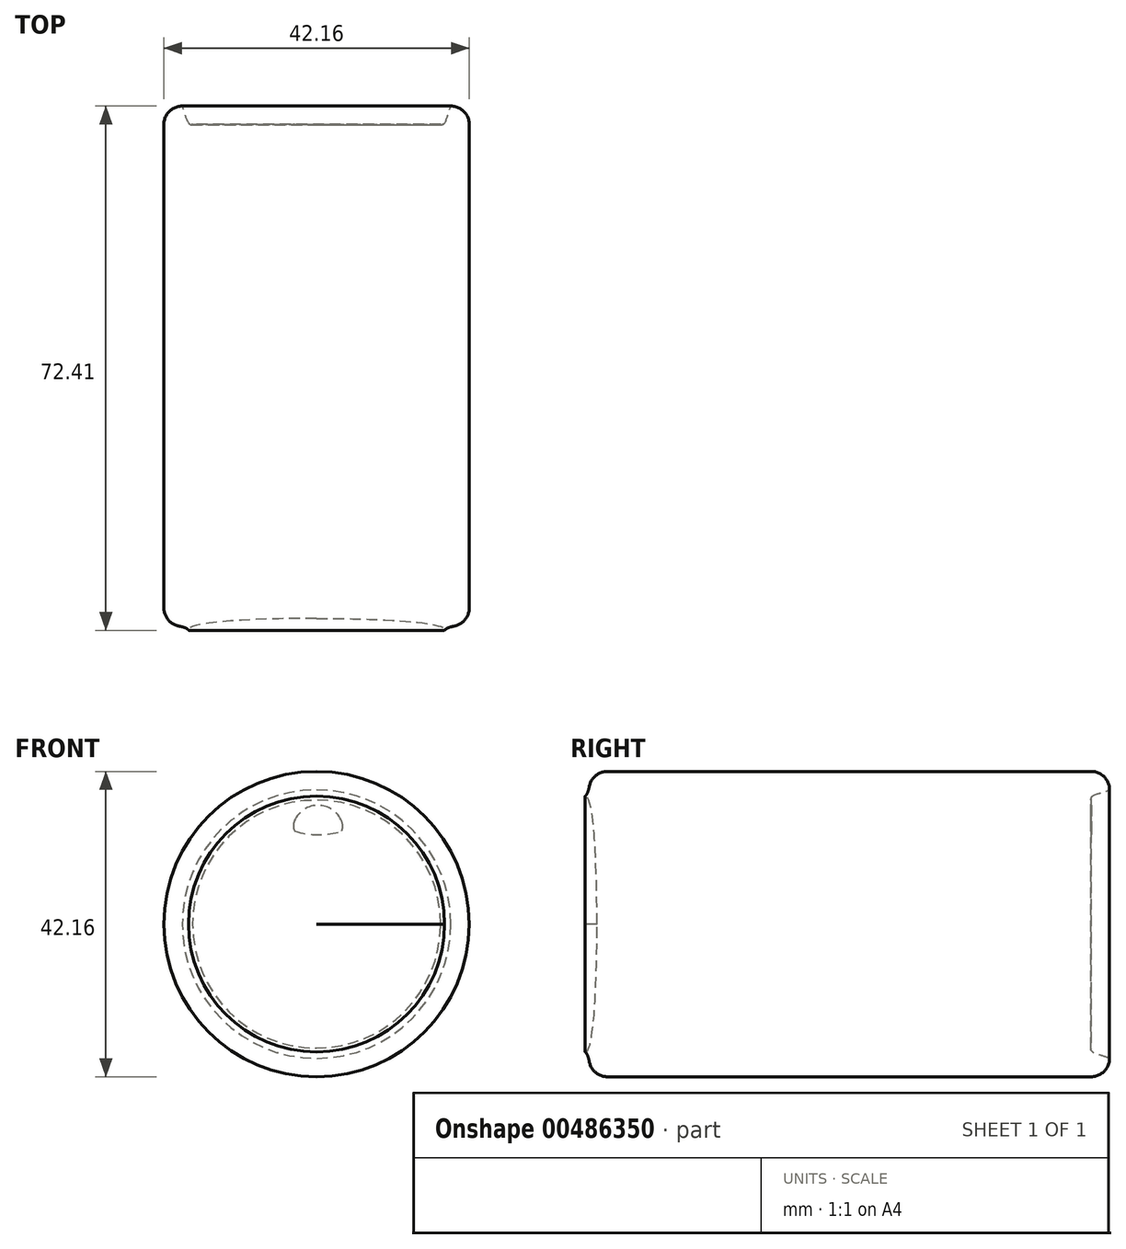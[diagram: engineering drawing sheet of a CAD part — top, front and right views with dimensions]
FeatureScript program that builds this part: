
annotation { "Feature Type Name" : "Feature", "Feature Type Description" : "" }
export const myFeature = defineFeature(function(context is Context, id is Id, definition is map)
    precondition{}
    {
        {
            var Q0;
            Q0=qCreatedBy(makeId("Top.planeOp"),FACE);
            var sketch = newSketch(context, id + "F0", { "sketchPlane" : qUnion([Q0])});
            skLineSegment(sketch, "E0", {"start": v(6.54, 1.64) * mm, "end": v(6.54, 69.87) * mm});
            skLineSegment(sketch, "E1", {"start": v(27.62, 69.87) * mm, "end": v(27.62, 3.08) * mm});
            skLineSegment(sketch, "E2", {"start": v(24.21, 0) * mm, "end": v(24.21, 0) * mm});
            skFitSpline(sketch, "E3", {"points": [v(6.54, 1.64) * mm, v(24.21, 0) * mm, v(23.02, -1.35) * mm], "startDerivative": vector(39.82, -0.08) * mm, "endDerivative": vector(-2.35, -7.4) * mm});
            skFitSpline(sketch, "E4", {"points": [v(27.62, 0.95) * mm, v(24.21, 0) * mm, v(24.63, -1.74) * mm], "startDerivative": vector(-5.23, -1.27) * mm, "endDerivative": vector(1.94, -4.17) * mm});
            skArc(sketch, "E5", {"start": v(23.27, -0.94) * mm, "mid": v(24.38, -1.1) * mm, "end": v(24.21, 0) * mm});
            skPoint(sketch, "E6.orphan", {"position": v(27.62, 0) * mm});
            skPoint(sketch, "E7.visualSharp", {"position": v(27.62, 71.14) * mm});
            skArc(sketch, "E7.filletArc", {"start": v(27.62, 69.87) * mm, "mid": v(26.88, 71.67) * mm, "end": v(25.08, 72.41) * mm});
            skArc(sketch, "E8.filletArc", {"start": v(25.59, 0.6) * mm, "mid": v(27.05, 1.48) * mm, "end": v(27.62, 3.08) * mm});
            skLineSegment(sketch, "E9.bottom", {"start": v(23.99, 69.87) * mm, "end": v(6.54, 69.87) * mm});
            skPoint(sketch, "E10.3.internal.snap0", {"position": v(25.08, 70.5) * mm});
            skFitSpline(sketch, "E10", {"points": [v(25.08, 72.41) * mm, v(23.99, 69.87) * mm, v(22.07, 70.8) * mm, v(20.14, 70.5) * mm], "startDerivative": vector(-3.04, -5.98) * mm, "endDerivative": vector(-5.69, -2.21) * mm});
            skPoint(sketch, "E9.left.end.orphan", {"position": v(25.08, 71.14) * mm});
            skSolve(sketch);
        }
        {
            var Q0;
            {var subQ1=sQuery(id+"F0.wireOp",EDGE,"E0");Q0=makeQuery(id+"F0.imprint","IMPRINT",FACE,{"disambiguationData":[TD([[makeQuery(id+"F0.imprint","IMPRINT",EDGE,{"derivedFrom":subQ1}),-1.0]])]});}
            var Q1;
            Q1=sQuery(id+"F0.wireOp",EDGE,"E0");
            revolve(context, id + "F1", {"entities" : qUnion([Q0]), "axis" : qUnion([Q1]), "revolveType" : RevolveType.FULL});
        }
        {
            var Q0;
            Q0=makeQuery(id+"F1.opRevolve","SWEPT_FACE",FACE,{"disambiguationData":[OSD([sQuery(id+"F0.wireOp",EDGE,"E9.bottom")])]});
            var sketch = newSketch(context, id + "F2", { "sketchPlane" : qUnion([Q0])});
            skArc(sketch, "E11", {"start": v(-3.5, 14.3) * mm, "mid": v(-6.8, 16.4) * mm, "end": v(-10.03, 14.2) * mm});
            skArc(sketch, "E12", {"start": v(-3.5, 12.85) * mm, "mid": v(-3.35, 13.58) * mm, "end": v(-3.5, 14.3) * mm});
            skArc(sketch, "E13", {"start": v(-10.03, 12.85) * mm, "mid": v(-6.76, 12.35) * mm, "end": v(-3.5, 12.85) * mm});
            skArc(sketch, "E14", {"start": v(-10.03, 14.2) * mm, "mid": v(-10.15, 13.53) * mm, "end": v(-10.03, 12.85) * mm});
            skSolve(sketch);
        }
        {
            var Q0;
            Q0=makeQuery(id+"F2.imprint","IMPRINT",FACE,{"disambiguationData":[TD([[makeQuery(id+"F2.imprint","IMPRINT",EDGE,{"derivedFrom":sQuery(id+"F2.wireOp",EDGE,"E11")}),1.0]])]});
            extrude(context, id + "F3", {"entities" : qUnion([Q0]), "operationType" : NewBodyOperationType.ADD, "depth" : 0.03 * mm});
        }
    });
